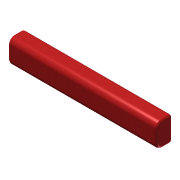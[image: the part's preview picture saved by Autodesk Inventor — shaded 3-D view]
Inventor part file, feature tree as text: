
AUTODESK INVENTOR PART (.ipt)
format: ipt  version: 2013 (Build 170138000, 138)  size: 120,832 bytes
history: native  units: in
note: dims shown in document units (in); Inventor stores cm internally (conversion verified against a paired STEP export)
features: extrude x3, sketch x3, projected_geometry x2, fillet x1
ambient origin geometry x8: Origin, YZ Plane, XZ Plane, XY Plane, X Axis, Y Axis, Z Axis, Center Point
bodies: Solid1 (feature_tree)
feature tree (9):
  extrude  "Extrusion1"  Depth=5.0in
  extrude  "Extrusion2"  Depth=2.5in
  extrude  "Extrusion3"  Depth=30.3in TaperAngle=0.0deg
  fillet  "Fillet1"  Radius=30.3in
  sketch  "Sketch1"  dims[d0=30.3in d1=5.0in]
  sketch  "Sketch2"  dims[d2=0.75in d3=0.0in d4=2.5in]
  sketch  "Sketch3"  dims[d5=2.5in d6=30.3in d7=0.0in d8=30.3in d9=0.0in d10=0.5in]
  projected_geometry  "Project Cut Edges1"
  projected_geometry  "Project Cut Edges2"
